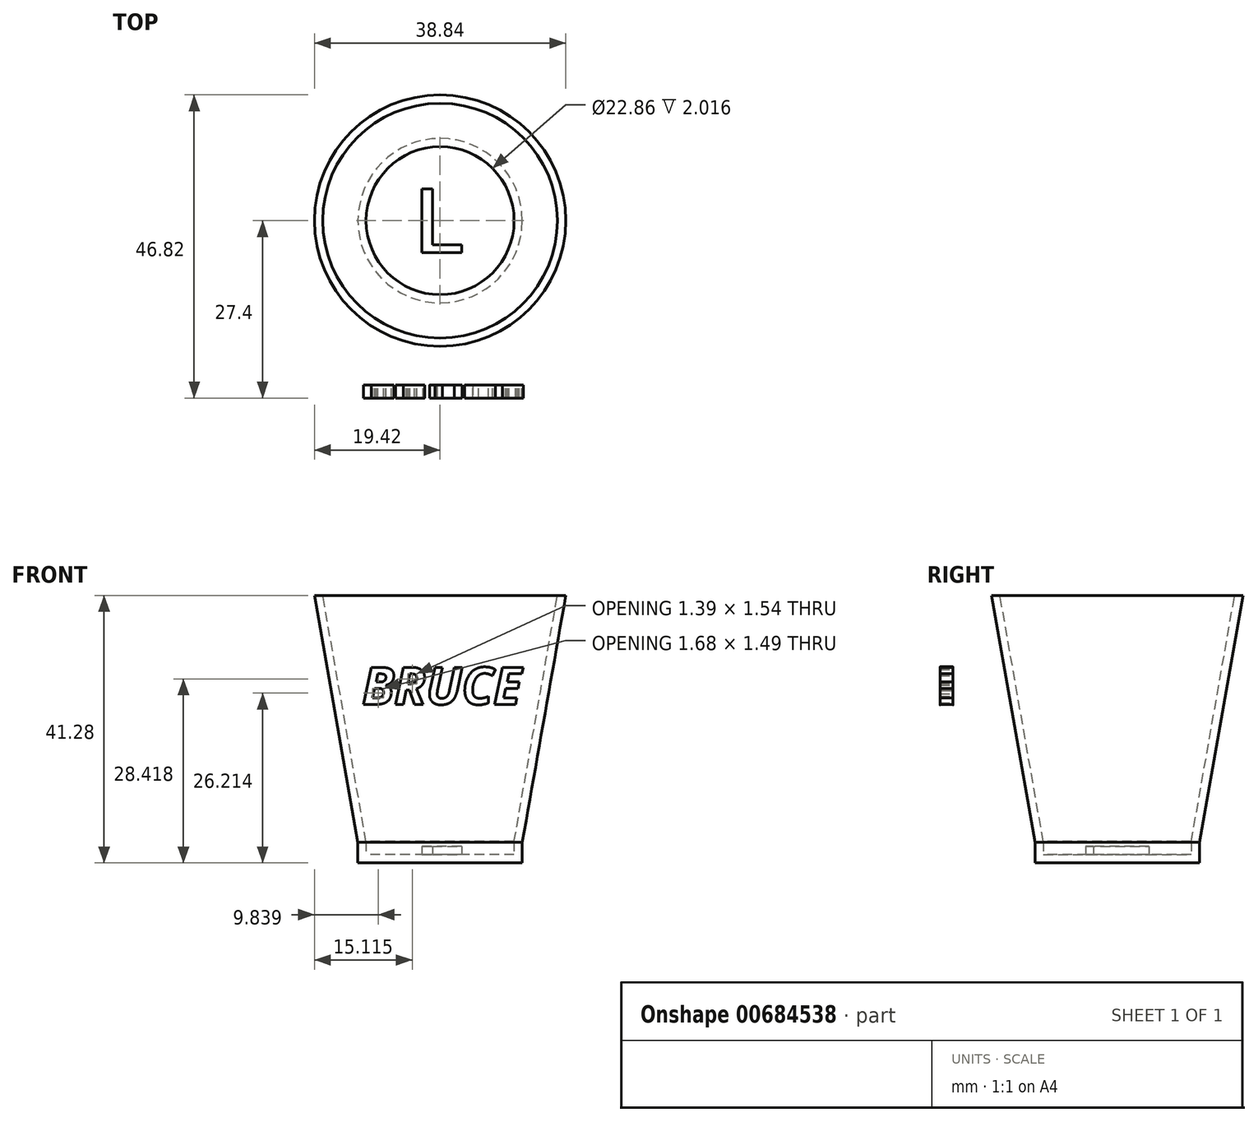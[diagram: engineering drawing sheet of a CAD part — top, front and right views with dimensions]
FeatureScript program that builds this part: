
annotation { "Feature Type Name" : "Feature", "Feature Type Description" : "" }
export const myFeature = defineFeature(function(context is Context, id is Id, definition is map)
    precondition{}
    {
        {
            var Q0;
            Q0=qCreatedBy(makeId("Top.planeOp"),FACE);
            var sketch = newSketch(context, id + "F0", { "sketchPlane" : qUnion([Q0])});
            skCircle(sketch, "E0", {"center": v(0, 0) * mm, "radius": 12.7 * mm});
            skSolve(sketch);
        }
        {
            var Q0;
            Q0=qSketchRegion(id+"F0",true);
            extrude(context, id + "F1", {"entities" : qUnion([Q0]), "depth" : 3.17 * mm});
        }
        {
            var Q0;
            Q0=makeQuery(id+"F1.opExtrude","CAP_FACE",FACE,{"disambiguationData":[OSD([sQuery(id+"F0.wireOp",EDGE,"E0")])],"isStart":false});
            var sketch = newSketch(context, id + "F2", { "sketchPlane" : qUnion([Q0])});
            skCircle(sketch, "E1", {"center": v(0, 0) * mm, "radius": 12.7 * mm});
            skSolve(sketch);
        }
        {
            var Q0;
            Q0=qSketchRegion(id+"F2",true);
            extrude(context, id + "F3", {"entities" : qUnion([Q0]), "operationType" : NewBodyOperationType.ADD, "depth" : 38.1 * mm, "hasDraft" : true, "draftAngle" : 10 * degree});
        }
        {
            var Q0;
            Q0=makeQuery(id+"F3.opExtrude","CAP_FACE",FACE,{"disambiguationData":[OSD([sQuery(id+"F2.wireOp",EDGE,"E1")])],"isStart":false});
            shell(context, id + "F4", {"entities" : qUnion([Q0]), "thickness" : 1.27 * mm});
        }
        {
            var Q0;
            {var subQ0=sQuery(id+"F0.wireOp",EDGE,"E0");Q0=makeQuery(id+"F4.opShell","OFFSET_FACE",FACE,{"disambiguationData":[OSD([subQ0]),TDD([makeQuery(id+"F1.opExtrude","CAP_FACE",FACE,{"disambiguationData":[OSD([subQ0])],"isStart":true})])]});}
            var sketch = newSketch(context, id + "F5", { "sketchPlane" : qUnion([Q0])});
            skText(sketch, "E2", { "text": "L", "fontName": "AllertaStencil-Regular.ttf"});
            const initialGuessF5  = {"E2": [-0.00405, -0.00491, 1, 0, 0.0098]};
            skSetInitialGuess(sketch, initialGuessF5);
            skSolve(sketch);
        }
        {
            var Q0;
            Q0=qSketchRegion(id+"F5",true);
            extrude(context, id + "F6", {"entities" : qUnion([Q0]), "operationType" : NewBodyOperationType.ADD, "depth" : 1.27 * mm});
        }
        {
            var Q0;
            Q0=qCreatedBy(makeId("Front.planeOp"),FACE);
            cPlane(context, id + "F7", {"entities" : qUnion([Q0]), "cplaneType" : CPlaneType.OFFSET, "offset" : 25.4 * mm, "width" : 152.4 * mm, "height" : 152.4 * mm});
        }
        {
            var Q0;
            Q0=qCreatedBy(id+"F7.planeOp",FACE);
            var sketch = newSketch(context, id + "F8", { "sketchPlane" : qUnion([Q0])});
            skText(sketch, "E3", { "text": "BRUCE", "fontName": "OpenSans-BoldItalic.ttf"});
            const initialGuessF8  = {"E3": [-0.01203, 0.02447, 1, 0, 0.00576]};
            skSetInitialGuess(sketch, initialGuessF8);
            skSolve(sketch);
        }
        {
            var Q0;
            Q0 = qSketchRegion(id + "F8", true);
            extrude(context, id + "F9", {"entities" : qUnion([Q0]), "depth" : 2 * mm, "offsetDistance" : 25.4 * mm});
        }
    });
